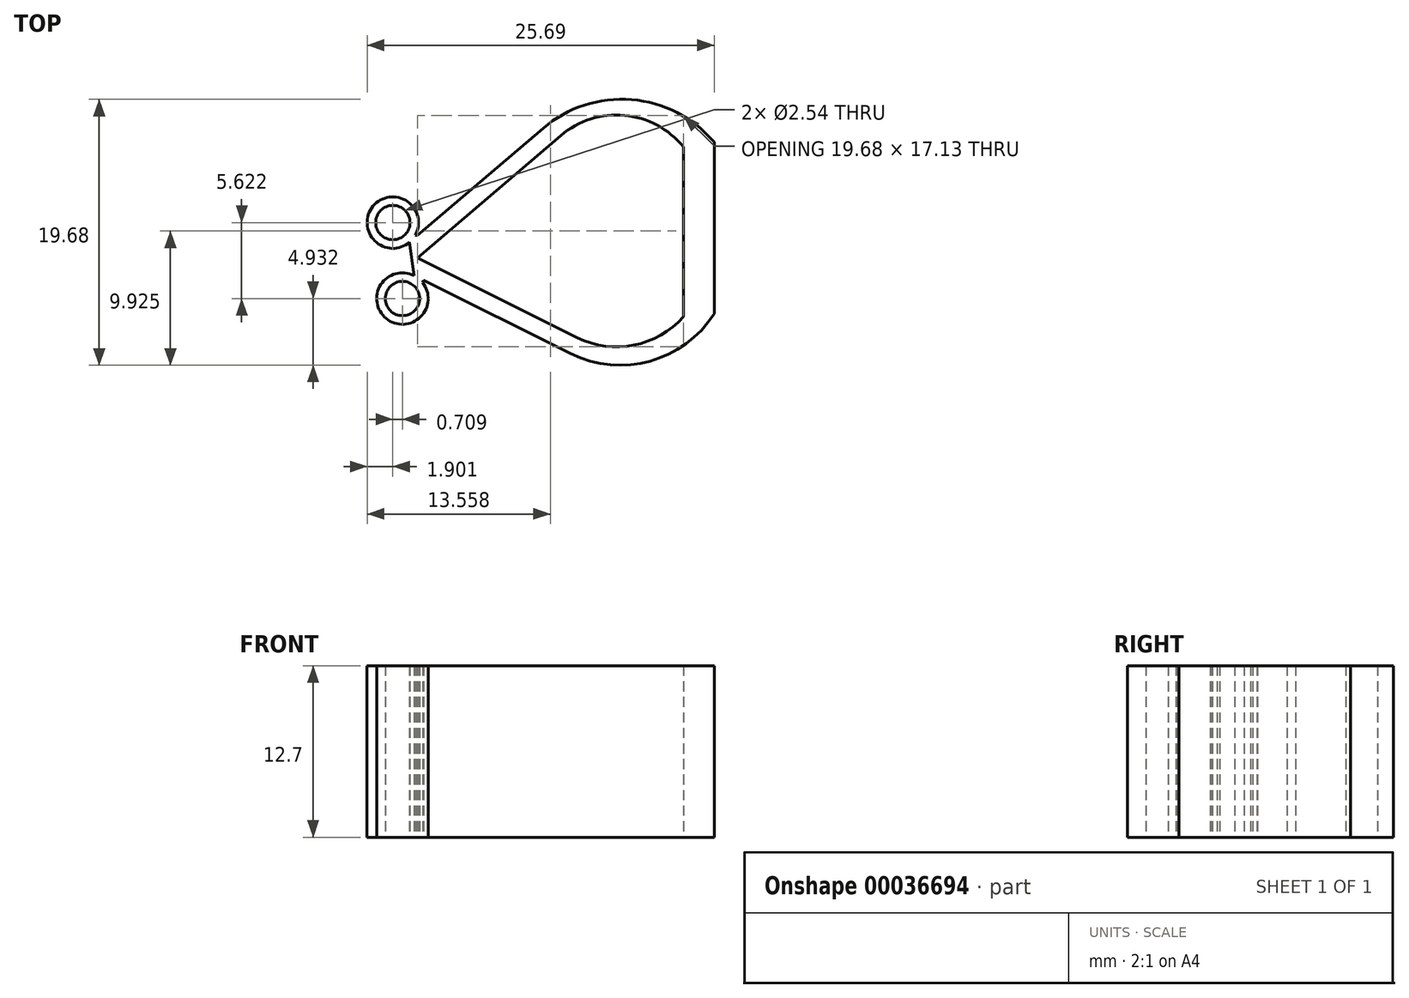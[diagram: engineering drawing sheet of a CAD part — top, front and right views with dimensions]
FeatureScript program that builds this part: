
annotation { "Feature Type Name" : "Feature", "Feature Type Description" : "" }
export const myFeature = defineFeature(function(context is Context, id is Id, definition is map)
    precondition{}
    {
        {
            var Q0;
            Q0=qCreatedBy(makeId("Top.planeOp"),FACE);
            var sketch = newSketch(context, id + "F0", { "sketchPlane" : qUnion([Q0])});
            skLineSegment(sketch, "E0", {"start": v(0, 0) * mm, "end": v(0, 12.57) * mm});
            skPoint(sketch, "E1", {"position": v(0, 6.29) * mm});
            skLineSegment(sketch, "E2", {"start": v(-19.68, 4.34) * mm, "end": v(-9.06, 13.4) * mm});
            skLineSegment(sketch, "E3", {"start": v(-19.68, 4.34) * mm, "end": v(-7.86, -1.54) * mm});
            skLineSegment(sketch, "E4", {"start": v(-19.7, 6) * mm, "end": v(-10.38, 13.95) * mm});
            skLineSegment(sketch, "E5", {"start": v(-19.22, 2.69) * mm, "end": v(-8.33, -2.73) * mm});
            skPoint(sketch, "E6", {"position": v(2.29, 6.57) * mm});
            skLineSegment(sketch, "E7", {"start": v(2.29, 0.22) * mm, "end": v(2.29, 12.92) * mm});
            skPoint(sketch, "E8", {"position": v(-9.84, 5.31) * mm});
            skPoint(sketch, "E8.positionSnap0", {"position": v(-9.84, 5.31) * mm});
            skArc(sketch, "E9", {"start": v(0, 12.57) * mm, "mid": v(-4.35, 14.9) * mm, "end": v(-9.06, 13.4) * mm});
            skArc(sketch, "E10", {"start": v(2.29, 12.92) * mm, "mid": v(-3.83, 16.07) * mm, "end": v(-10.38, 13.95) * mm});
            skArc(sketch, "E11", {"start": v(-7.86, -1.54) * mm, "mid": v(-3.67, -2.1) * mm, "end": v(0, 0) * mm});
            skArc(sketch, "E12", {"start": v(-8.33, -2.73) * mm, "mid": v(-2.45, -3.3) * mm, "end": v(2.29, 0.22) * mm});
            skArc(sketch, "E13", {"start": v(-19.84, 6.03) * mm, "mid": v(-22.97, 8.18) * mm, "end": v(-20.26, 5.52) * mm});
            skPoint(sketch, "E14", {"position": v(-20.26, 5.52) * mm});
            skArc(sketch, "E15", {"start": v(-19.94, 3.05) * mm, "mid": v(-21.99, -0.14) * mm, "end": v(-19.3, 2.53) * mm});
            skPoint(sketch, "E16", {"position": v(-19.94, 3.05) * mm});
            skPoint(sketch, "E17.orphan", {"position": v(-21.97, 4.06) * mm});
            skLineSegment(sketch, "E18", {"start": v(-20.26, 5.52) * mm, "end": v(-19.94, 3.05) * mm});
            skCircle(sketch, "E19", {"center": v(-21.5, 6.96) * mm, "radius": 1.27 * mm});
            skCircle(sketch, "E20", {"center": v(-20.79, 1.34) * mm, "radius": 1.27 * mm});
            skLineSegment(sketch, "E21", {"start": v(-19.84, 6.03) * mm, "end": v(-19.7, 6) * mm});
            skLineSegment(sketch, "E22", {"start": v(-19.3, 2.53) * mm, "end": v(-19.22, 2.69) * mm});
            skSolve(sketch);
        }
        {
            var Q0;
            Q0=makeQuery(id+"F0.imprint","IMPRINT",FACE,{"disambiguationData":[TD([[makeQuery(id+"F0.imprint","IMPRINT",EDGE,{"derivedFrom":sQuery(id+"F0.wireOp",EDGE,"E15")}),1.0]])]});
            var Q1;
            Q1=makeQuery(id+"F0.imprint","IMPRINT",FACE,{"disambiguationData":[TD([[makeQuery(id+"F0.imprint","IMPRINT",EDGE,{"derivedFrom":sQuery(id+"F0.wireOp",EDGE,"E13")}),1.0]])]});
            extrude(context, id + "F1", {"entities" : qUnion([Q0, Q1]), "depth" : 12.7 * mm});
        }
    });
